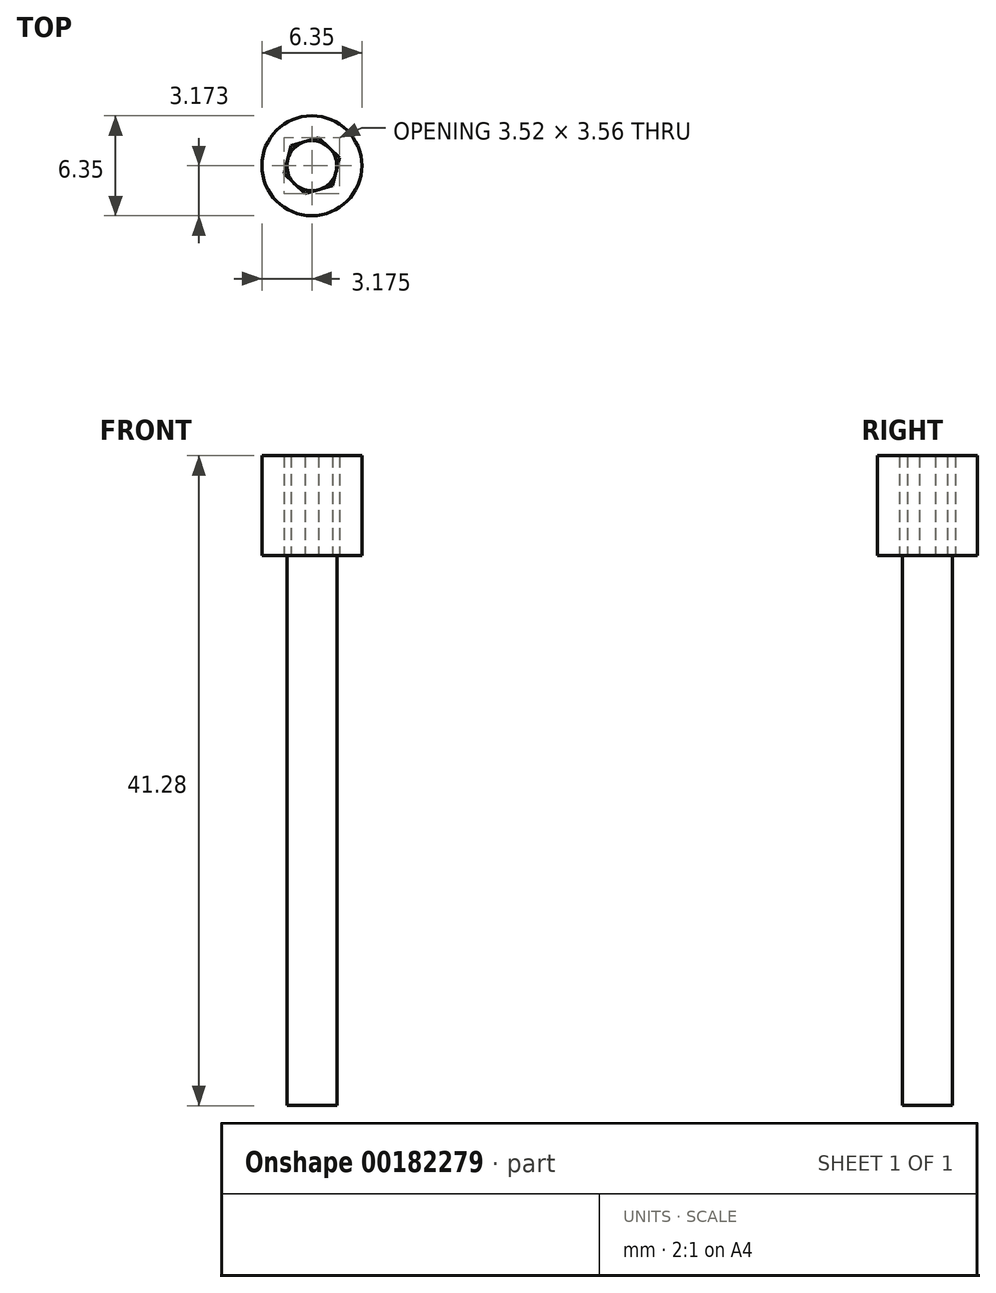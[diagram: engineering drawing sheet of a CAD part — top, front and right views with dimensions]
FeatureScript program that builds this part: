
annotation { "Feature Type Name" : "Feature", "Feature Type Description" : "" }
export const myFeature = defineFeature(function(context is Context, id is Id, definition is map)
    precondition{}
    {
        {
            var Q0;
            Q0=qCreatedBy(makeId("Top.planeOp"),FACE);
            var sketch = newSketch(context, id + "F0", { "sketchPlane" : qUnion([Q0])});
            skCircle(sketch, "E0", {"center": v(-31.43, 22.61) * mm, "radius": 3.18 * mm});
            skCircle(sketch, "E1.cCircle", {"center": v(-31.43, 22.61) * mm, "radius": 1.59 * mm, "construction": true});
            skLineSegment(sketch, "E1.0", {"start": v(-32.76, 23.88) * mm, "end": v(-31, 24.4) * mm});
            skLineSegment(sketch, "E1.1", {"start": v(-31, 24.4) * mm, "end": v(-29.68, 23.13) * mm});
            skLineSegment(sketch, "E1.2", {"start": v(-29.68, 23.13) * mm, "end": v(-30.1, 21.35) * mm});
            skLineSegment(sketch, "E1.3", {"start": v(-30.1, 21.35) * mm, "end": v(-31.87, 20.83) * mm});
            skLineSegment(sketch, "E1.4", {"start": v(-31.87, 20.83) * mm, "end": v(-33.2, 22.1) * mm});
            skLineSegment(sketch, "E1.5", {"start": v(-33.2, 22.1) * mm, "end": v(-32.76, 23.88) * mm});
            skPoint(sketch, "E1.0.midPoint", {"position": v(-31.88, 24.14) * mm});
            skSolve(sketch);
        }
        {
            var Q0;
            Q0 = qSketchRegion(id + "F0", true);
            extrude(context, id + "F1", {"entities" : qUnion([Q0]), "depth" : 6.35 * mm});
        }
        {
            var Q0;
            Q0=makeQuery(id+"F1.opExtrude","CAP_FACE",FACE,{"disambiguationData":[OSD([sQuery(id+"F0.wireOp",EDGE,"E0"),sQuery(id+"F0.wireOp",EDGE,"E1.0"),sQuery(id+"F0.wireOp",EDGE,"E1.1"),sQuery(id+"F0.wireOp",EDGE,"E1.2"),sQuery(id+"F0.wireOp",EDGE,"E1.3"),sQuery(id+"F0.wireOp",EDGE,"E1.4"),sQuery(id+"F0.wireOp",EDGE,"E1.5")])],"isStart":true});
            var sketch = newSketch(context, id + "F2", { "sketchPlane" : qUnion([Q0])});
            skCircle(sketch, "E2", {"center": v(-31.43, -22.61) * mm, "radius": 1.59 * mm});
            skSolve(sketch);
        }
        {
            var Q0;
            Q0 = qSketchRegion(id + "F2", true);
            extrude(context, id + "F3", {"entities" : qUnion([Q0]), "depth" : 34.92 * mm});
        }
    });
